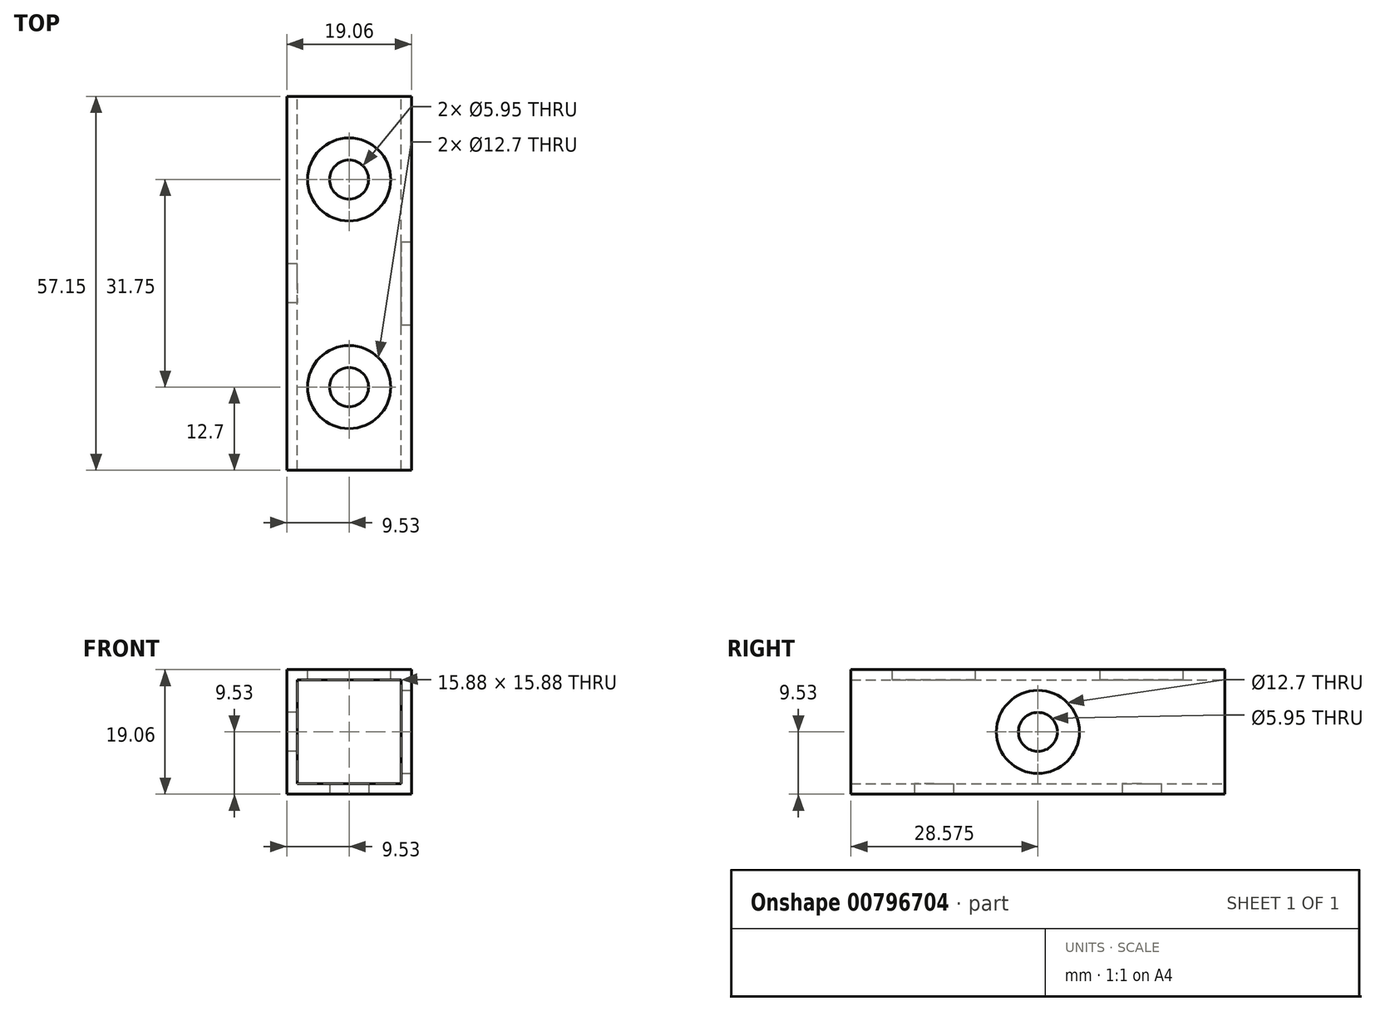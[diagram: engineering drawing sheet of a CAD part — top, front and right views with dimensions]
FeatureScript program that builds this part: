
annotation { "Feature Type Name" : "Feature", "Feature Type Description" : "" }
export const myFeature = defineFeature(function(context is Context, id is Id, definition is map)
    precondition{}
    {
        {
            var Q0;
            Q0=qCreatedBy(makeId("Front.planeOp"),FACE);
            var sketch = newSketch(context, id + "F0", { "sketchPlane" : qUnion([Q0])});
            skLineSegment(sketch, "E0.bottom", {"start": v(-9.52, 9.53) * mm, "end": v(9.53, 9.53) * mm});
            skLineSegment(sketch, "E0.top", {"start": v(-9.53, -9.53) * mm, "end": v(9.52, -9.53) * mm});
            skLineSegment(sketch, "E0.left", {"start": v(-9.52, 9.53) * mm, "end": v(-9.53, -9.52) * mm});
            skLineSegment(sketch, "E0.right", {"start": v(9.53, 9.53) * mm, "end": v(9.52, -9.52) * mm});
            skPoint(sketch, "E0.middle", {"position": v(0, 0) * mm});
            skLineSegment(sketch, "E1.bottom", {"start": v(-7.94, 7.94) * mm, "end": v(7.94, 7.94) * mm});
            skLineSegment(sketch, "E1.top", {"start": v(-7.94, -7.94) * mm, "end": v(7.94, -7.94) * mm});
            skLineSegment(sketch, "E1.left", {"start": v(-7.94, 7.94) * mm, "end": v(-7.94, -7.94) * mm});
            skLineSegment(sketch, "E1.right", {"start": v(7.94, 7.94) * mm, "end": v(7.94, -7.94) * mm});
            skSolve(sketch);
        }
        {
            var Q0;
            Q0 = qSketchRegion(id + "F0", true);
            extrude(context, id + "F1", {"entities" : qUnion([Q0]), "depth" : 57.15 * mm, "offsetDistance" : 25.4 * mm});
        }
        {
            var Q0;
            Q0=makeQuery(id+"F1.opExtrude","SWEPT_FACE",FACE,{"disambiguationData":[OSD([sQuery(id+"F0.wireOp",EDGE,"E0.top")])]});
            var sketch = newSketch(context, id + "F2", { "sketchPlane" : qUnion([Q0])});
            skPoint(sketch, "E2", {"position": v(0, 44.45) * mm});
            skPoint(sketch, "E3", {"position": v(0, 12.7) * mm});
            skSolve(sketch);
        }
        {
            var Q0;
            Q0=sQuery(id+"F2.wireOp",VERTEX,"E2");
            var Q1;
            Q1=sQuery(id+"F2.wireOp",VERTEX,"E3");
            var Q2;
            Q2=makeQuery(id+"F1.opExtrude","SWEPT_BODY",BODY,{"disambiguationData":[OSD([sQuery(id+"F0.wireOp",EDGE,"E0.bottom"),sQuery(id+"F0.wireOp",EDGE,"E0.top"),sQuery(id+"F0.wireOp",EDGE,"E0.left"),sQuery(id+"F0.wireOp",EDGE,"E0.right"),sQuery(id+"F0.wireOp",EDGE,"E1.bottom"),sQuery(id+"F0.wireOp",EDGE,"E1.top"),sQuery(id+"F0.wireOp",EDGE,"E1.left"),sQuery(id+"F0.wireOp",EDGE,"E1.right")])]});
            hole(context, id + "F3", {"style" : HoleStyle.SIMPLE, "endStyle" : HoleEndStyle.BLIND, "holeDiameter" : 5.95 * mm, "majorDiameter" : 2.18 * mm, "holeDepth" : 6.35 * mm, "isTappedThrough" : true, "tappedDepth" : 12.7 * mm, "tapClearance" : 3, "startFromSketch" : true, "locations" : qUnion([Q0, Q1]), "scope" : qUnion([Q2])});
        }
        {
            var Q0;
            Q0=makeQuery(id+"F1.opExtrude","SWEPT_FACE",FACE,{"disambiguationData":[OSD([sQuery(id+"F0.wireOp",EDGE,"E0.bottom")])]});
            var sketch = newSketch(context, id + "F4", { "sketchPlane" : qUnion([Q0])});
            skPoint(sketch, "E4", {"position": v(0, -12.7) * mm});
            skPoint(sketch, "E5", {"position": v(0, -162.85) * mm});
            skPoint(sketch, "E6", {"position": v(0, -44.45) * mm});
            skSolve(sketch);
        }
        {
            var Q0;
            Q0=sQuery(id+"F4.wireOp",VERTEX,"E4");
            var Q1;
            Q1=sQuery(id+"F4.wireOp",VERTEX,"E6");
            var Q2;
            Q2=makeQuery(id+"F1.opExtrude","SWEPT_BODY",BODY,{"disambiguationData":[OSD([sQuery(id+"F0.wireOp",EDGE,"E0.bottom"),sQuery(id+"F0.wireOp",EDGE,"E0.top"),sQuery(id+"F0.wireOp",EDGE,"E0.left"),sQuery(id+"F0.wireOp",EDGE,"E0.right"),sQuery(id+"F0.wireOp",EDGE,"E1.bottom"),sQuery(id+"F0.wireOp",EDGE,"E1.top"),sQuery(id+"F0.wireOp",EDGE,"E1.left"),sQuery(id+"F0.wireOp",EDGE,"E1.right")])]});
            hole(context, id + "F5", {"style" : HoleStyle.SIMPLE, "endStyle" : HoleEndStyle.BLIND, "holeDiameter" : 12.7 * mm, "majorDiameter" : 6.35 * mm, "holeDepth" : 6.35 * mm, "isTappedThrough" : true, "tappedDepth" : 12.7 * mm, "tapClearance" : 3, "startFromSketch" : true, "locations" : qUnion([Q0, Q1]), "scope" : qUnion([Q2])});
        }
        {
            var Q0;
            Q0=makeQuery(id+"F1.opExtrude","SWEPT_FACE",FACE,{"disambiguationData":[OSD([sQuery(id+"F0.wireOp",EDGE,"E0.right")])]});
            var sketch = newSketch(context, id + "F6", { "sketchPlane" : qUnion([Q0])});
            skPoint(sketch, "E7", {"position": v(-28.58, 0) * mm});
            skSolve(sketch);
        }
        {
            var Q0;
            Q0=sQuery(id+"F6.wireOp",VERTEX,"E7");
            var Q1;
            Q1=makeQuery(id+"F1.opExtrude","SWEPT_BODY",BODY,{"disambiguationData":[OSD([sQuery(id+"F0.wireOp",EDGE,"E0.bottom"),sQuery(id+"F0.wireOp",EDGE,"E0.top"),sQuery(id+"F0.wireOp",EDGE,"E0.left"),sQuery(id+"F0.wireOp",EDGE,"E0.right"),sQuery(id+"F0.wireOp",EDGE,"E1.bottom"),sQuery(id+"F0.wireOp",EDGE,"E1.top"),sQuery(id+"F0.wireOp",EDGE,"E1.left"),sQuery(id+"F0.wireOp",EDGE,"E1.right")])]});
            hole(context, id + "F7", {"style" : HoleStyle.SIMPLE, "endStyle" : HoleEndStyle.BLIND, "holeDiameter" : 12.7 * mm, "majorDiameter" : 6.35 * mm, "holeDepth" : 6.35 * mm, "isTappedThrough" : true, "tappedDepth" : 12.7 * mm, "tapClearance" : 3, "startFromSketch" : true, "locations" : qUnion([Q0]), "scope" : qUnion([Q1])});
        }
        {
            var Q0;
            Q0=makeQuery(id+"F1.opExtrude","SWEPT_FACE",FACE,{"disambiguationData":[OSD([sQuery(id+"F0.wireOp",EDGE,"E0.left")])]});
            var sketch = newSketch(context, id + "F8", { "sketchPlane" : qUnion([Q0])});
            skPoint(sketch, "E8", {"position": v(28.58, 0) * mm});
            skSolve(sketch);
        }
        {
            var Q0;
            Q0=sQuery(id+"F8.wireOp",VERTEX,"E8");
            var Q1;
            Q1=makeQuery(id+"F1.opExtrude","SWEPT_BODY",BODY,{"disambiguationData":[OSD([sQuery(id+"F0.wireOp",EDGE,"E0.bottom"),sQuery(id+"F0.wireOp",EDGE,"E0.top"),sQuery(id+"F0.wireOp",EDGE,"E0.left"),sQuery(id+"F0.wireOp",EDGE,"E0.right"),sQuery(id+"F0.wireOp",EDGE,"E1.bottom"),sQuery(id+"F0.wireOp",EDGE,"E1.top"),sQuery(id+"F0.wireOp",EDGE,"E1.left"),sQuery(id+"F0.wireOp",EDGE,"E1.right")])]});
            hole(context, id + "F9", {"style" : HoleStyle.SIMPLE, "endStyle" : HoleEndStyle.BLIND, "holeDiameter" : 5.95 * mm, "majorDiameter" : 6.35 * mm, "holeDepth" : 6.35 * mm, "isTappedThrough" : true, "tappedDepth" : 12.7 * mm, "tapClearance" : 3, "startFromSketch" : true, "locations" : qUnion([Q0]), "scope" : qUnion([Q1])});
        }
    });
